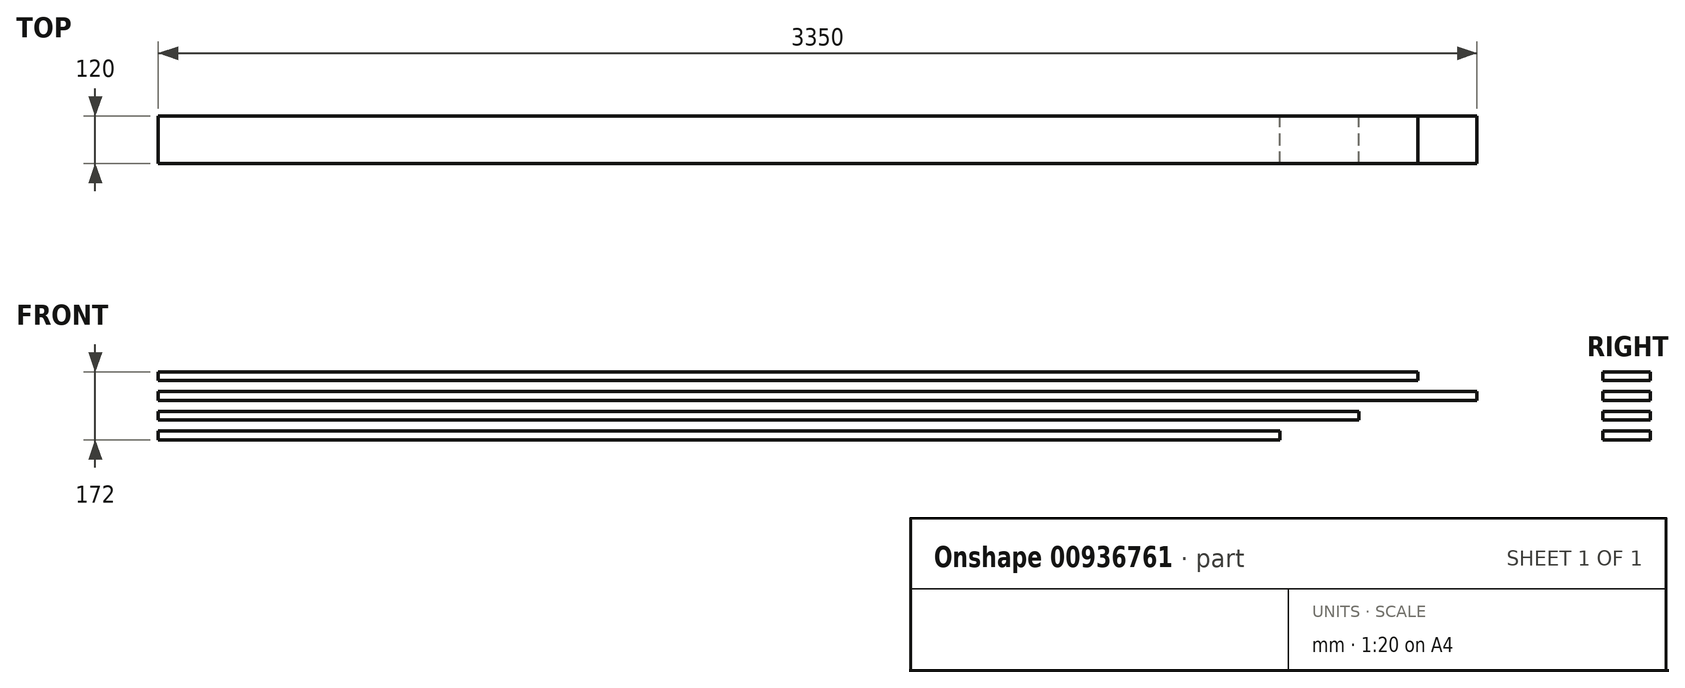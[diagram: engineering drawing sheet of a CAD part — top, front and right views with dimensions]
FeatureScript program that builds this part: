
annotation { "Feature Type Name" : "Feature", "Feature Type Description" : "" }
export const myFeature = defineFeature(function(context is Context, id is Id, definition is map)
    precondition{}
    {
        {
            var Q0;
            Q0=qCreatedBy(makeId("Right.planeOp"),FACE);
            var sketch = newSketch(context, id + "F0", { "sketchPlane" : qUnion([Q0])});
            skLineSegment(sketch, "E0.bottom", {"start": v(0, 0) * mm, "end": v(120, 0) * mm});
            skLineSegment(sketch, "E0.top", {"start": v(0, 22) * mm, "end": v(120, 22) * mm});
            skLineSegment(sketch, "E0.left", {"start": v(0, 0) * mm, "end": v(0, 22) * mm});
            skLineSegment(sketch, "E0.right", {"start": v(120, 0) * mm, "end": v(120, 22) * mm});
            skLineSegment(sketch, "E1.0.1.0", {"start": v(0, 50) * mm, "end": v(0, 72) * mm});
            skLineSegment(sketch, "E1.0.1.1", {"start": v(0, 72) * mm, "end": v(120, 72) * mm});
            skLineSegment(sketch, "E1.0.1.2", {"start": v(0, 50) * mm, "end": v(120, 50) * mm});
            skLineSegment(sketch, "E1.0.1.3", {"start": v(120, 50) * mm, "end": v(120, 72) * mm});
            skLineSegment(sketch, "E1.0.2.0", {"start": v(0, 100) * mm, "end": v(0, 122) * mm});
            skLineSegment(sketch, "E1.0.2.1", {"start": v(0, 122) * mm, "end": v(120, 122) * mm});
            skLineSegment(sketch, "E1.0.2.2", {"start": v(0, 100) * mm, "end": v(120, 100) * mm});
            skLineSegment(sketch, "E1.0.2.3", {"start": v(120, 100) * mm, "end": v(120, 122) * mm});
            skLineSegment(sketch, "E1.0.3.0", {"start": v(0, 150) * mm, "end": v(0, 172) * mm});
            skLineSegment(sketch, "E1.0.3.1", {"start": v(0, 172) * mm, "end": v(120, 172) * mm});
            skLineSegment(sketch, "E1.0.3.2", {"start": v(0, 150) * mm, "end": v(120, 150) * mm});
            skLineSegment(sketch, "E1.0.3.3", {"start": v(120, 150) * mm, "end": v(120, 172) * mm});
            skLineSegment(sketch, "E1.0.4.0", {"start": v(0, 200) * mm, "end": v(0, 222) * mm});
            skLineSegment(sketch, "E1.0.4.1", {"start": v(0, 222) * mm, "end": v(120, 222) * mm});
            skLineSegment(sketch, "E1.0.4.2", {"start": v(0, 200) * mm, "end": v(120, 200) * mm});
            skLineSegment(sketch, "E1.0.4.3", {"start": v(120, 200) * mm, "end": v(120, 222) * mm});
            skLineSegment(sketch, "E1.0.5.0", {"start": v(0, 250) * mm, "end": v(0, 272) * mm});
            skLineSegment(sketch, "E1.0.5.1", {"start": v(0, 272) * mm, "end": v(120, 272) * mm});
            skLineSegment(sketch, "E1.0.5.2", {"start": v(0, 250) * mm, "end": v(120, 250) * mm});
            skLineSegment(sketch, "E1.0.5.3", {"start": v(120, 250) * mm, "end": v(120, 272) * mm});
            skLineSegment(sketch, "E1.0.6.0", {"start": v(0, 300) * mm, "end": v(0, 322) * mm});
            skLineSegment(sketch, "E1.0.6.1", {"start": v(0, 322) * mm, "end": v(120, 322) * mm});
            skLineSegment(sketch, "E1.0.6.2", {"start": v(0, 300) * mm, "end": v(120, 300) * mm});
            skLineSegment(sketch, "E1.0.6.3", {"start": v(120, 300) * mm, "end": v(120, 322) * mm});
            skLineSegment(sketch, "E1.0.7.0", {"start": v(0, 350) * mm, "end": v(0, 372) * mm});
            skLineSegment(sketch, "E1.0.7.1", {"start": v(0, 372) * mm, "end": v(120, 372) * mm});
            skLineSegment(sketch, "E1.0.7.2", {"start": v(0, 350) * mm, "end": v(120, 350) * mm});
            skLineSegment(sketch, "E1.0.7.3", {"start": v(120, 350) * mm, "end": v(120, 372) * mm});
            skLineSegment(sketch, "E1.0.8.0", {"start": v(0, 400) * mm, "end": v(0, 422) * mm});
            skLineSegment(sketch, "E1.0.8.1", {"start": v(0, 422) * mm, "end": v(120, 422) * mm});
            skLineSegment(sketch, "E1.0.8.2", {"start": v(0, 400) * mm, "end": v(120, 400) * mm});
            skLineSegment(sketch, "E1.0.8.3", {"start": v(120, 400) * mm, "end": v(120, 422) * mm});
            skLineSegment(sketch, "E1.0.9.0", {"start": v(0, 450) * mm, "end": v(0, 472) * mm});
            skLineSegment(sketch, "E1.0.9.1", {"start": v(0, 472) * mm, "end": v(120, 472) * mm});
            skLineSegment(sketch, "E1.0.9.2", {"start": v(0, 450) * mm, "end": v(120, 450) * mm});
            skLineSegment(sketch, "E1.0.9.3", {"start": v(120, 450) * mm, "end": v(120, 472) * mm});
            skLineSegment(sketch, "E1.direction1", {"start": v(0, 0) * mm, "end": v(25, 0) * mm, "construction": true});
            skLineSegment(sketch, "E1.direction2", {"start": v(0, 0) * mm, "end": v(0, 50) * mm, "construction": true});
            skSolve(sketch);
        }
        {
            var Q0;
            Q0=makeQuery(id+"F0.imprint","IMPRINT",FACE,{"disambiguationData":[TD([[makeQuery(id+"F0.imprint","IMPRINT",EDGE,{"derivedFrom":sQuery(id+"F0.wireOp",EDGE,"E0.bottom")}),1.0]])]});
            extrude(context, id + "F1", {"entities" : qUnion([Q0]), "depth" : 2850 * mm, "offsetDistance" : 25 * mm});
        }
        {
            var Q0;
            Q0=makeQuery(id+"F0.imprint","IMPRINT",FACE,{"disambiguationData":[TD([[makeQuery(id+"F0.imprint","IMPRINT",EDGE,{"derivedFrom":sQuery(id+"F0.wireOp",EDGE,"E1.0.1.0")}),-1.0]])]});
            extrude(context, id + "F2", {"entities" : qUnion([Q0]), "depth" : 3050 * mm, "offsetDistance" : 25 * mm});
        }
        {
            var Q0;
            Q0=makeQuery(id+"F0.imprint","IMPRINT",FACE,{"disambiguationData":[TD([[makeQuery(id+"F0.imprint","IMPRINT",EDGE,{"derivedFrom":sQuery(id+"F0.wireOp",EDGE,"E1.0.2.0")}),-1.0]])]});
            extrude(context, id + "F3", {"entities" : qUnion([Q0]), "depth" : 3350 * mm, "offsetDistance" : 25 * mm});
        }
        {
            var Q0;
            Q0=makeQuery(id+"F0.imprint","IMPRINT",FACE,{"disambiguationData":[TD([[makeQuery(id+"F0.imprint","IMPRINT",EDGE,{"derivedFrom":sQuery(id+"F0.wireOp",EDGE,"E1.0.3.0")}),-1.0]])]});
            extrude(context, id + "F4", {"entities" : qUnion([Q0]), "depth" : 3200 * mm, "offsetDistance" : 25 * mm});
        }
    });
